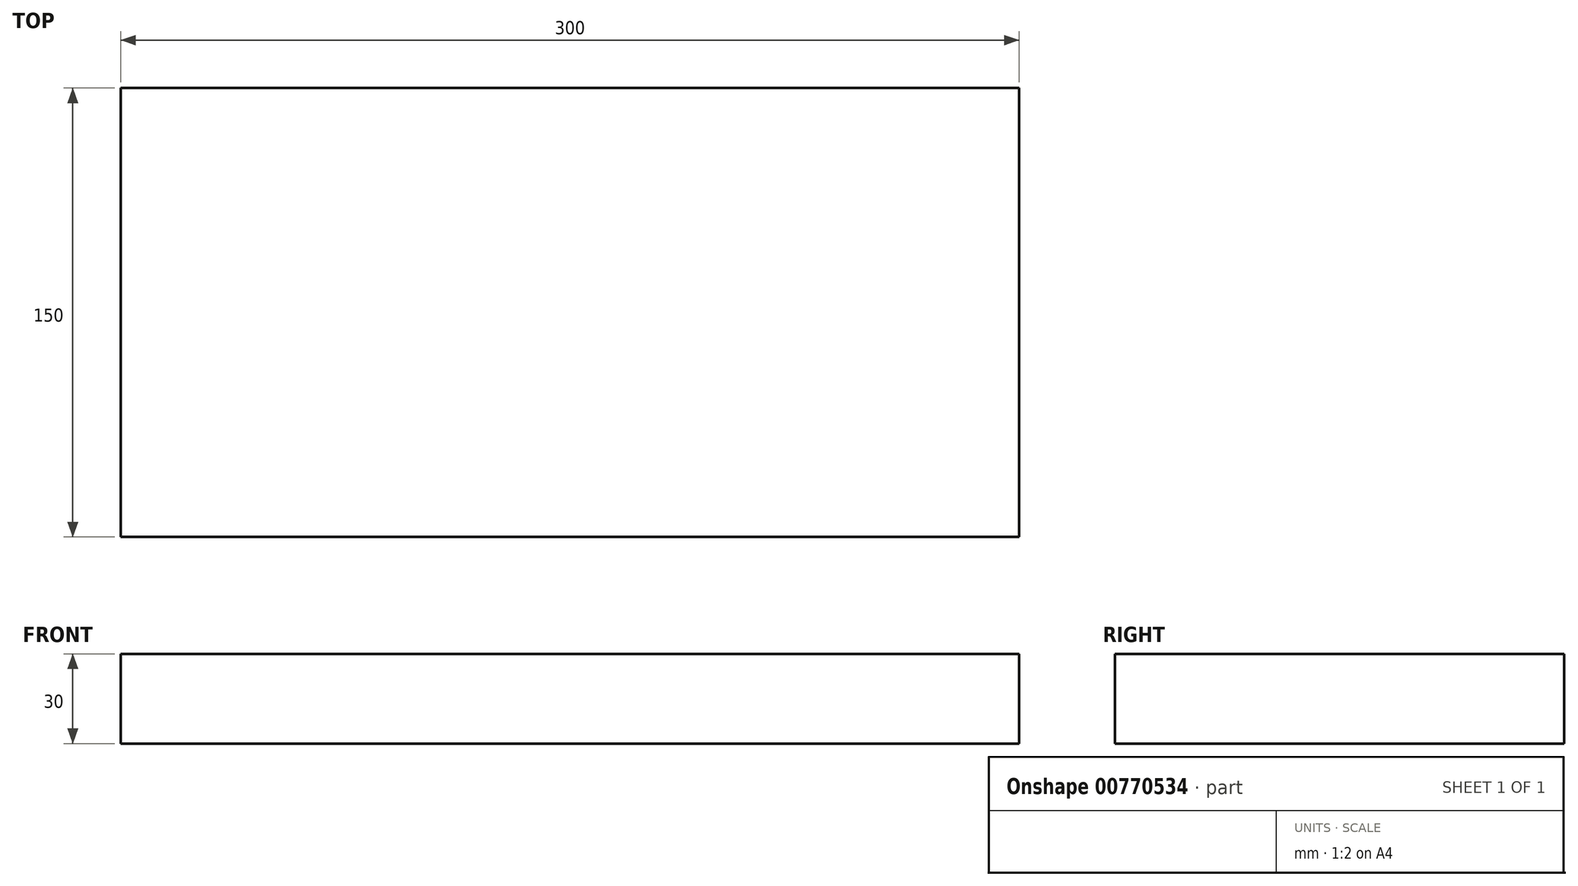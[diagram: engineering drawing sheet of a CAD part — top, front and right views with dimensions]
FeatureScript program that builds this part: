
annotation { "Feature Type Name" : "Feature", "Feature Type Description" : "" }
export const myFeature = defineFeature(function(context is Context, id is Id, definition is map)
    precondition{}
    {
        {
            var Q0;
            Q0=qCreatedBy(makeId("Right.planeOp"),FACE);
            var sketch = newSketch(context, id + "F0", { "sketchPlane" : qUnion([Q0])});
            skLineSegment(sketch, "E0.bottom", {"start": v(-2.8, 29.1) * mm, "end": v(147.2, 29.1) * mm});
            skLineSegment(sketch, "E0.top", {"start": v(-2.8, -0.9) * mm, "end": v(147.2, -0.9) * mm});
            skLineSegment(sketch, "E0.left", {"start": v(-2.8, 29.1) * mm, "end": v(-2.8, -0.9) * mm});
            skLineSegment(sketch, "E0.right", {"start": v(147.2, 29.1) * mm, "end": v(147.2, -0.9) * mm});
            skLineSegment(sketch, "E1", {"start": v(-2.98, 29.87) * mm, "end": v(-41.3, 36.42) * mm});
            skLineSegment(sketch, "E2", {"start": v(-41.3, 36.42) * mm, "end": v(-41.1, 5.85) * mm});
            skLineSegment(sketch, "E3", {"start": v(-41.1, 5.85) * mm, "end": v(-2.8, -0.9) * mm});
            skSolve(sketch);
        }
        {
            var Q0;
            Q0=makeQuery(id+"F0.imprint","IMPRINT",FACE,{"disambiguationData":[TD([[makeQuery(id+"F0.imprint","IMPRINT",EDGE,{"derivedFrom":sQuery(id+"F0.wireOp",EDGE,"E0.bottom")}),-1.0]])]});
            extrude(context, id + "F1", {"entities" : qUnion([Q0]), "endBound" : BoundingType.SYMMETRIC, "depth" : 300 * mm, "offsetDistance" : 25 * mm});
        }
    });
